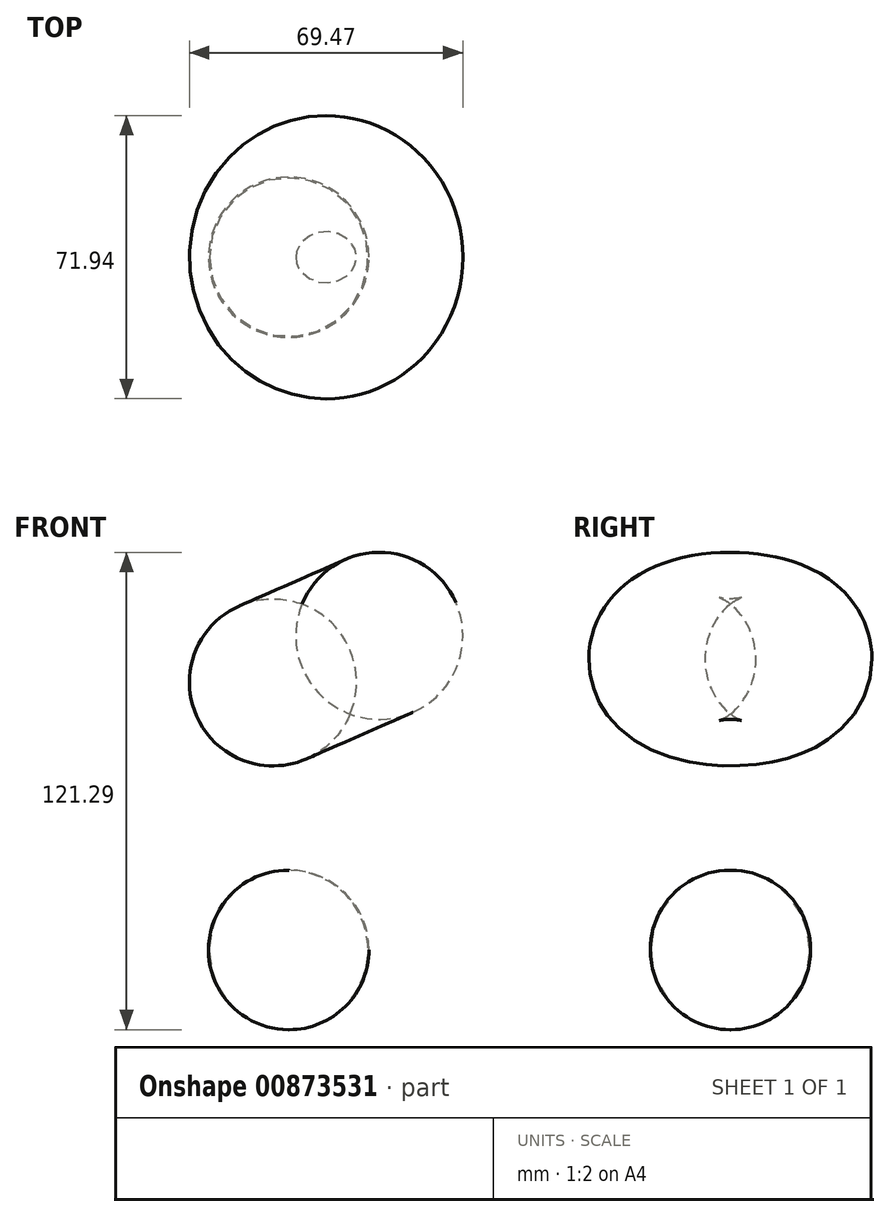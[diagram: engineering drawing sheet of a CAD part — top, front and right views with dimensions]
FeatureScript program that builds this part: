
annotation { "Feature Type Name" : "Feature", "Feature Type Description" : "" }
export const myFeature = defineFeature(function(context is Context, id is Id, definition is map)
    precondition{}
    {
        {
            var Q0;
            Q0=qCreatedBy(makeId("Front.planeOp"),FACE);
            var sketch = newSketch(context, id + "F0", { "sketchPlane" : qUnion([Q0])});
            skArc(sketch, "E0", {"start": v(-33.56, 52.54) * mm, "mid": v(-33.38, 35.96) * mm, "end": v(-21.33, 24.58) * mm});
            skLineSegment(sketch, "E1", {"start": v(-33.56, 52.54) * mm, "end": v(-21.33, 24.58) * mm});
            skSolve(sketch);
        }
        {
            var Q0;
            Q0 = qSketchRegion(id + "F0", true);
            var Q1;
            Q1=sQuery(id+"F0.wireOp",EDGE,"E1");
            revolve(context, id + "F1", {"surfaceOperationType" : NewSurfaceOperationType.NEW, "entities" : qUnion([Q0]), "axis" : qUnion([Q1]), "revolveType" : RevolveType.FULL});
        }
        {
            var Q0;
            Q0=qCreatedBy(makeId("Front.planeOp"),FACE);
            var sketch = newSketch(context, id + "F2", { "sketchPlane" : qUnion([Q0])});
            skArc(sketch, "E2", {"start": v(-37.3, -55.6) * mm, "mid": v(-16.58, -35.5) * mm, "end": v(-36.95, -15.07) * mm});
            skLineSegment(sketch, "E3", {"start": v(-36.95, 0) * mm, "end": v(-36.95, -70.14) * mm});
            skSolve(sketch);
        }
        {
            var Q0;
            {var subQ0=sQuery(id+"F2.wireOp",EDGE,"E3");var subQ1=sQuery(id+"F2.wireOp",EDGE,"E2");var subQ2=makeQuery(id+"F2.imprint","INTERSECT",VERTEX,{"disambiguationData":[OD(0.0)],"derivedFrom":[subQ1,subQ0]});Q0=makeQuery(id+"F2.imprint","IMPRINT",FACE,{"disambiguationData":[TD([[makeQuery(id+"F2.imprint","IMPRINT",EDGE,{"disambiguationData":[TD([[subQ2,1.0]])],"derivedFrom":subQ1}),1.0]])]});}
            var Q1;
            Q1=sQuery(id+"F2.wireOp",EDGE,"E3");
            revolve(context, id + "F3", {"surfaceOperationType" : NewSurfaceOperationType.NEW, "entities" : qUnion([Q0]), "axis" : qUnion([Q1]), "revolveType" : RevolveType.FULL});
        }
    });
